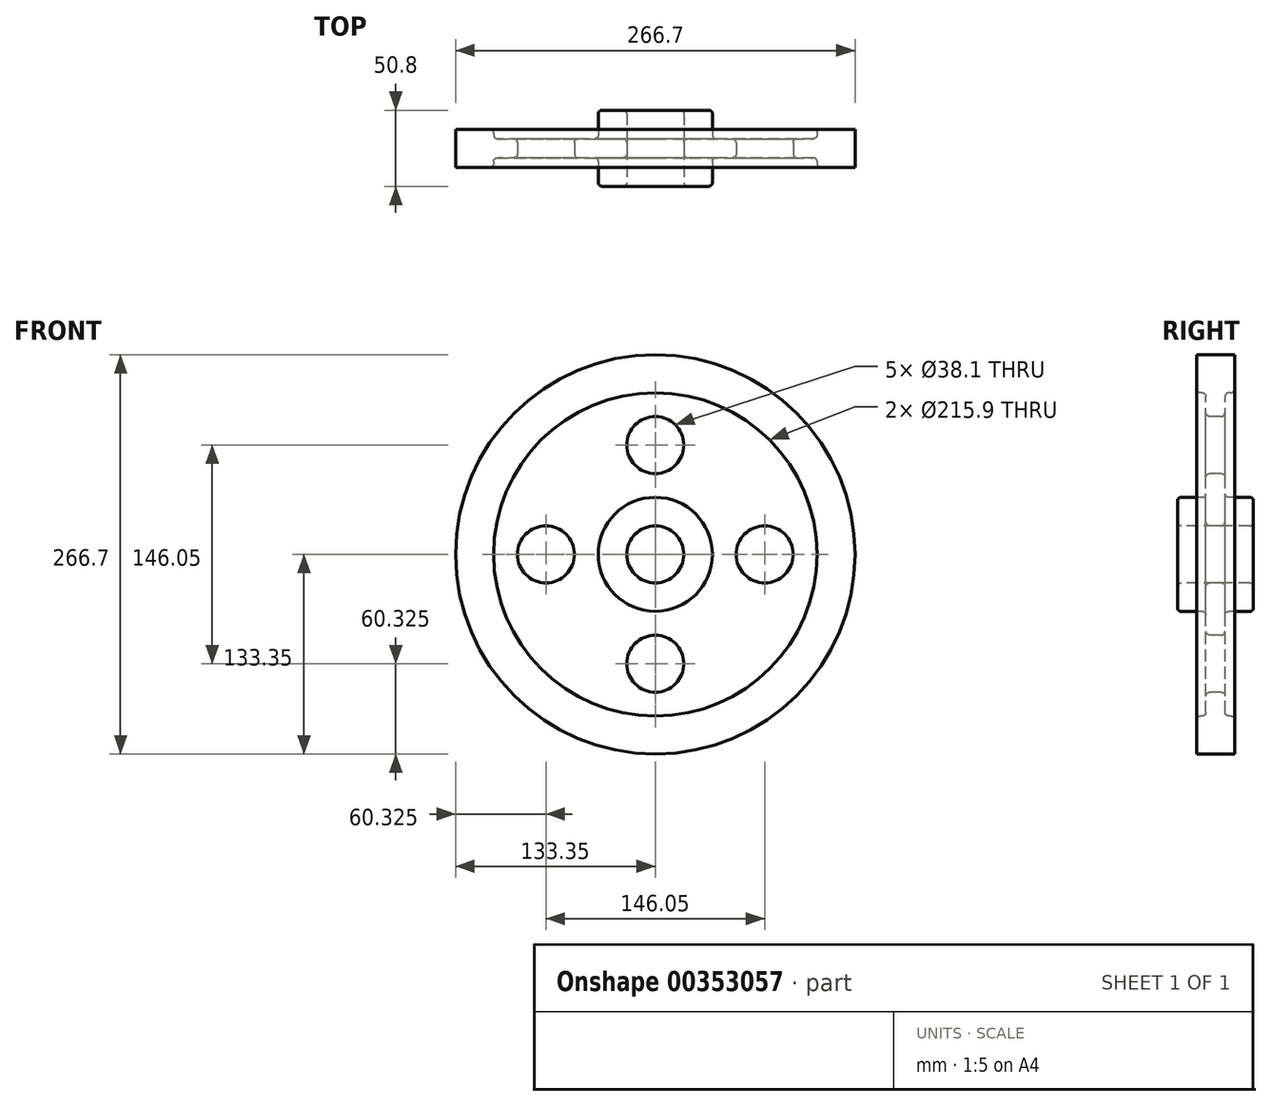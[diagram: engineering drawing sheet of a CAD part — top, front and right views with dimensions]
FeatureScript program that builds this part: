
annotation { "Feature Type Name" : "Feature", "Feature Type Description" : "" }
export const myFeature = defineFeature(function(context is Context, id is Id, definition is map)
    precondition{}
    {
        {
            var Q0;
            Q0=qCreatedBy(makeId("Right.planeOp"),FACE);
            var sketch = newSketch(context, id + "F0", { "sketchPlane" : qUnion([Q0])});
            skLineSegment(sketch, "E0", {"start": v(0, 0) * mm, "end": v(6.35, 0) * mm, "construction": true});
            skLineSegment(sketch, "E1.0", {"start": v(6.35, 38.1) * mm, "end": v(25.4, 38.1) * mm});
            skLineSegment(sketch, "E2.0", {"start": v(6.35, 107.95) * mm, "end": v(12.7, 107.95) * mm});
            skLineSegment(sketch, "E3.0", {"start": v(0, 133.35) * mm, "end": v(12.7, 133.35) * mm});
            skLineSegment(sketch, "E4.0", {"start": v(25.4, 19.05) * mm, "end": v(25.4, 38.1) * mm});
            skLineSegment(sketch, "E5.0", {"start": v(6.35, 38.1) * mm, "end": v(6.35, 107.95) * mm});
            skLineSegment(sketch, "E6.trimOffspring", {"start": v(12.7, 107.95) * mm, "end": v(12.7, 133.35) * mm});
            skLineSegment(sketch, "E7", {"start": v(0, 133.35) * mm, "end": v(0, 19.05) * mm, "construction": true});
            skLineSegment(sketch, "E8.MirrorCS", {"start": v(-12.7, 107.95) * mm, "end": v(-12.7, 133.35) * mm});
            skLineSegment(sketch, "E9.MirrorCS", {"start": v(0, 133.35) * mm, "end": v(-12.7, 133.35) * mm});
            skLineSegment(sketch, "E10.MirrorCS", {"start": v(-6.35, 107.95) * mm, "end": v(-12.7, 107.95) * mm});
            skLineSegment(sketch, "E11.MirrorCS", {"start": v(-6.35, 38.1) * mm, "end": v(-6.35, 107.95) * mm});
            skLineSegment(sketch, "E12.MirrorCS", {"start": v(-6.35, 38.1) * mm, "end": v(-25.4, 38.1) * mm});
            skLineSegment(sketch, "E13.MirrorCS", {"start": v(-25.4, 19.05) * mm, "end": v(-25.4, 38.1) * mm});
            skLineSegment(sketch, "E14.MirrorCS", {"start": v(-6.35, 0) * mm, "end": v(-12.7, 0) * mm, "construction": true});
            skPoint(sketch, "E15.orphan", {"position": v(6.35, 0) * mm});
            skPoint(sketch, "E16.orphan", {"position": v(12.7, 0) * mm});
            skPoint(sketch, "E17.0.end.orphan", {"position": v(12.7, 38.1) * mm});
            skPoint(sketch, "E18.orphan", {"position": v(-12.7, 38.1) * mm});
            skPoint(sketch, "E19.MirrorCS.start.orphan", {"position": v(-6.35, 0) * mm});
            skPoint(sketch, "E20.MirrorCS.start.orphan", {"position": v(-12.7, 0) * mm});
            skPoint(sketch, "E21.orphan", {"position": v(-6.35, 133.35) * mm});
            skPoint(sketch, "E22.orphan", {"position": v(6.35, 133.35) * mm});
            skPoint(sketch, "E23.0.start.orphan", {"position": v(0, 19.05) * mm});
            skPoint(sketch, "E24.orphan", {"position": v(0, 38.1) * mm});
            skPoint(sketch, "E25.orphan", {"position": v(0, 107.95) * mm});
            skLineSegment(sketch, "E26", {"start": v(-12.7, 0) * mm, "end": v(6.35, 0) * mm});
            skLineSegment(sketch, "E27", {"start": v(-25.4, 19.05) * mm, "end": v(25.4, 19.05) * mm});
            skLineSegment(sketch, "E28.trimOffspring", {"start": v(12.7, 0) * mm, "end": v(25.4, 0) * mm});
            skPoint(sketch, "E29.orphan", {"position": v(-25.4, 0) * mm});
            skPoint(sketch, "E30.orphan", {"position": v(0, 0) * mm});
            skSolve(sketch);
        }
        {
            var Q0;
            Q0 = qSketchRegion(id + "F0", true);
            var Q1;
            Q1=sQuery(id+"F0.wireOp",EDGE,"E26");
            revolve(context, id + "F1", {"entities" : qUnion([Q0]), "axis" : qUnion([Q1]), "revolveType" : RevolveType.FULL});
        }
        {
            var Q0;
            Q0=makeQuery(id+"F1.opRevolve","SWEPT_FACE",FACE,{"disambiguationData":[OSD([sQuery(id+"F0.wireOp",EDGE,"E11.MirrorCS")])]});
            var sketch = newSketch(context, id + "F2", { "sketchPlane" : qUnion([Q0])});
            skLineSegment(sketch, "E31", {"start": v(0, 0) * mm, "end": v(0, 73.03) * mm});
            skCircle(sketch, "E32", {"center": v(0, 73.03) * mm, "radius": 19.05 * mm});
            skCircle(sketch, "E33.1.0", {"center": v(-73.03, 0) * mm, "radius": 19.05 * mm});
            skCircle(sketch, "E33.2.0", {"center": v(0, -73.03) * mm, "radius": 19.05 * mm});
            skCircle(sketch, "E33.3.0", {"center": v(73.03, 0) * mm, "radius": 19.05 * mm});
            skPoint(sketch, "E33.center", {"position": v(0, 0) * mm});
            skSolve(sketch);
        }
        {
            var Q0;
            Q0=makeQuery(id+"F2.imprint","IMPRINT",FACE,{"disambiguationData":[TD([[makeQuery(id+"F2.imprint","IMPRINT",EDGE,{"derivedFrom":sQuery(id+"F2.wireOp",EDGE,"E32")}),1.0]])]});
            var Q1;
            Q1=makeQuery(id+"F2.imprint","IMPRINT",FACE,{"disambiguationData":[TD([[makeQuery(id+"F2.imprint","IMPRINT",EDGE,{"derivedFrom":sQuery(id+"F2.wireOp",EDGE,"E33.1.0")}),1.0]])]});
            var Q2;
            Q2=makeQuery(id+"F2.imprint","IMPRINT",FACE,{"disambiguationData":[TD([[makeQuery(id+"F2.imprint","IMPRINT",EDGE,{"derivedFrom":sQuery(id+"F2.wireOp",EDGE,"E33.2.0")}),1.0]])]});
            var Q3;
            Q3=makeQuery(id+"F2.imprint","IMPRINT",FACE,{"disambiguationData":[TD([[makeQuery(id+"F2.imprint","IMPRINT",EDGE,{"derivedFrom":sQuery(id+"F2.wireOp",EDGE,"E33.3.0")}),1.0]])]});
            extrude(context, id + "F3", {"entities" : qUnion([Q0, Q1, Q2, Q3]), "operationType" : NewBodyOperationType.REMOVE, "oppositeDirection" : true, "depth" : 25.4 * mm});
        }
        {
            var Q0;
            Q0=makeQuery(id+"F1.opRevolve","SWEPT_FACE",FACE,{"disambiguationData":[OSD([sQuery(id+"F0.wireOp",EDGE,"E10.MirrorCS")])]});
            var Q1;
            Q1=makeQuery(id+"F1.opRevolve","SWEPT_FACE",FACE,{"disambiguationData":[OSD([sQuery(id+"F0.wireOp",EDGE,"E11.MirrorCS")])]});
            var Q2;
            Q2=makeQuery(id+"F1.opRevolve","SWEPT_FACE",FACE,{"disambiguationData":[OSD([sQuery(id+"F0.wireOp",EDGE,"E12.MirrorCS")])]});
            var Q3;
            Q3=makeQuery(id+"F1.opRevolve","SWEPT_FACE",FACE,{"disambiguationData":[OSD([sQuery(id+"F0.wireOp",EDGE,"E13.MirrorCS")])]});
            fillet(context, id + "F4", {"entities" : qUnion([Q0, Q1, Q2, Q3]), "radius" : 2.54 * mm, "tangentPropagation" : true, "allowEdgeOverflow" : false});
        }
        {
            var Q0;
            Q0=makeQuery(id+"F1.opRevolve","SWEPT_FACE",FACE,{"disambiguationData":[OSD([sQuery(id+"F0.wireOp",EDGE,"E2.0")])]});
            var Q1;
            Q1=makeQuery(id+"F1.opRevolve","SWEPT_FACE",FACE,{"disambiguationData":[OSD([sQuery(id+"F0.wireOp",EDGE,"E5.0")])]});
            var Q2;
            Q2=makeQuery(id+"F1.opRevolve","SWEPT_FACE",FACE,{"disambiguationData":[OSD([sQuery(id+"F0.wireOp",EDGE,"E1.0")])]});
            var Q3;
            Q3=makeQuery(id+"F1.opRevolve","SWEPT_FACE",FACE,{"disambiguationData":[OSD([sQuery(id+"F0.wireOp",EDGE,"E4.0")])]});
            fillet(context, id + "F5", {"entities" : qUnion([Q0, Q1, Q2, Q3]), "radius" : 2.54 * mm, "tangentPropagation" : true, "allowEdgeOverflow" : false});
        }
    });
